# Revit family: 00870010
name_source: partatom
category: Plumbing Fixtures
revit_build: Autodesk Revit 2016 (Build: 20150220_1215(x64)
units: mm (PartAtom-declared; Revit-internal decimal feet)

## family parameters
Always vertical = Yes
Cut with Voids When Loaded = No
OmniClass Number = 23.45.55.00
OmniClass Title = Sanitary Faucets, Wastes
Part Type = Normal
Room Calculation Point = No
Round Connector Dimension = Use Diameter
Shared = No
Work Plane-Based = No

## types (1)
- 00870010 Washbasin faucet
    2D/3D/BIM Files URL = http://static.hansa.com
    Advanced Features = Adjustable settings (with magnetic key)
    Aerator = Pressure controlled aerator;Laminar;HONEYCOMB®;Burglarproof
    AssetType = Fixed
    Automatic Flush = off (off/12/24/48/72 h)
    Automatic Flush Period = 30 s (10/30/60/120/180/240/300/600 s)
    BIMObjectName = 00870010
    Battery = AA 1.5 V Lithium x 2
    BodyMaterial = Brass
    Brand = Hansa
    Catalog Drawing URL = http://static.hansa.com
    Category = Public & Semi-public
    Class = Battery-operated, touchless
    CloseOffRating = 0
    Color = Chrome
    Connection = Threaded connection
    Connection Size = G1/2
    ConvergoRefNr = 0087-1809-0149-FI
    Customs Code = 84818019
    DN Size = DN15
    Dimension Drawing URL = http://static.hansa.com
    DurationUnit = Year
    EAN Number = 4057304000010
    EMC Directive = 2014/30/EU
    Electronic Parts = Low battery indication, solenoid valve
    FDV Document URL = http://www.hansa.com
    FaucetMainMaterial = Brass
    Features = Battery-operated, touchless
    Finish = Polished
    Flow Drawing URL = http://static.hansa.com
    Flow Rate At 300kPa With Flow Controller = 0.1 L/s
    FlowCoefficient = 0
    Group = Washbasin faucets
    Health Sales Arguments = Touch-free operation. Maximum comfort, maximum hygiene.
    IfcExportAs = IfcValveType
    IfcExportType = FAUCET
    Installation Type = Wall-mounted
    Installation and Maintenance = http://static.hansa.com
    Intelligent After Flow Period = 2 s ± 1 s (1/2/3/4/8 s)
    ManufacterURL = http://www.hansa.com
    Manufacturer = Hansa
    ManufacturerName = Hansa
    Market = AUT;BEL;CZE;DEU;ESP;FRA;INT;ITA;NLD;SVK
    Material = Brass
    Max Flow Period = 120.0 s
    Mechanical Parts = Shut-off valve
    Model = 00870010 Washbasin faucet
    ModelReference = 00870010
    Mounting Holes = 1 mounting hole
    NBSDescription = Water supply fittings for baths
    NBSReference = 45-35-70/315
    Name = 00870010 Washbasin faucet
    Name_en = 00870010 Washbasin faucet
    NominalDepth = 215 mm
    NominalHeight = 75 mm
    NominalWidth = 75 mm
    Operating Voltage = 3 V
    Package Weight = 1.234 kg
    Package external Dimensions = 240 x 85 x 66
    Product Code = 00870010
    Product Datasheet = http://www.hansa.com
    Product Family = HANSAELECTRA
    Product Image URL = http://static.hansa.com
    Product URL = http://static.hansa.com
    Projection = 175 mm
    Protection Class = IP 55
    Recognition Range = ~15 cm (~10/15/17/20 cm)
    Revision = 2
    Shape = Sculptured
    Size = 75x215x75 mm
    Spare Parts = http://static.hansa.com
    Spout Type = Fixed spout
    Temperature = Preset water temperature
    Uniclass2 = Pr_40_30_96_07
    Uniclass2015Description = Bath manual water supply sets
    Uniclass2015Reference = Pr_40_20_87_07
    Usage Group = Offices, personnel sanitary facilities;Toilets for the Disabled;Pharmacies, Opticians, Dentists;Health centers & Child welfare clinics;Hospitals;Food stores;Gas stations;Schools
    Version = 2
    VersionDate = 01/01/2019
    WarrantyDescription = http://warranty.hansa.com
    WarrantyDurationUnit = Year

## geometry (parser evidence)
native form markers: Sweep x6
no freeform markers — native parametric forms only
